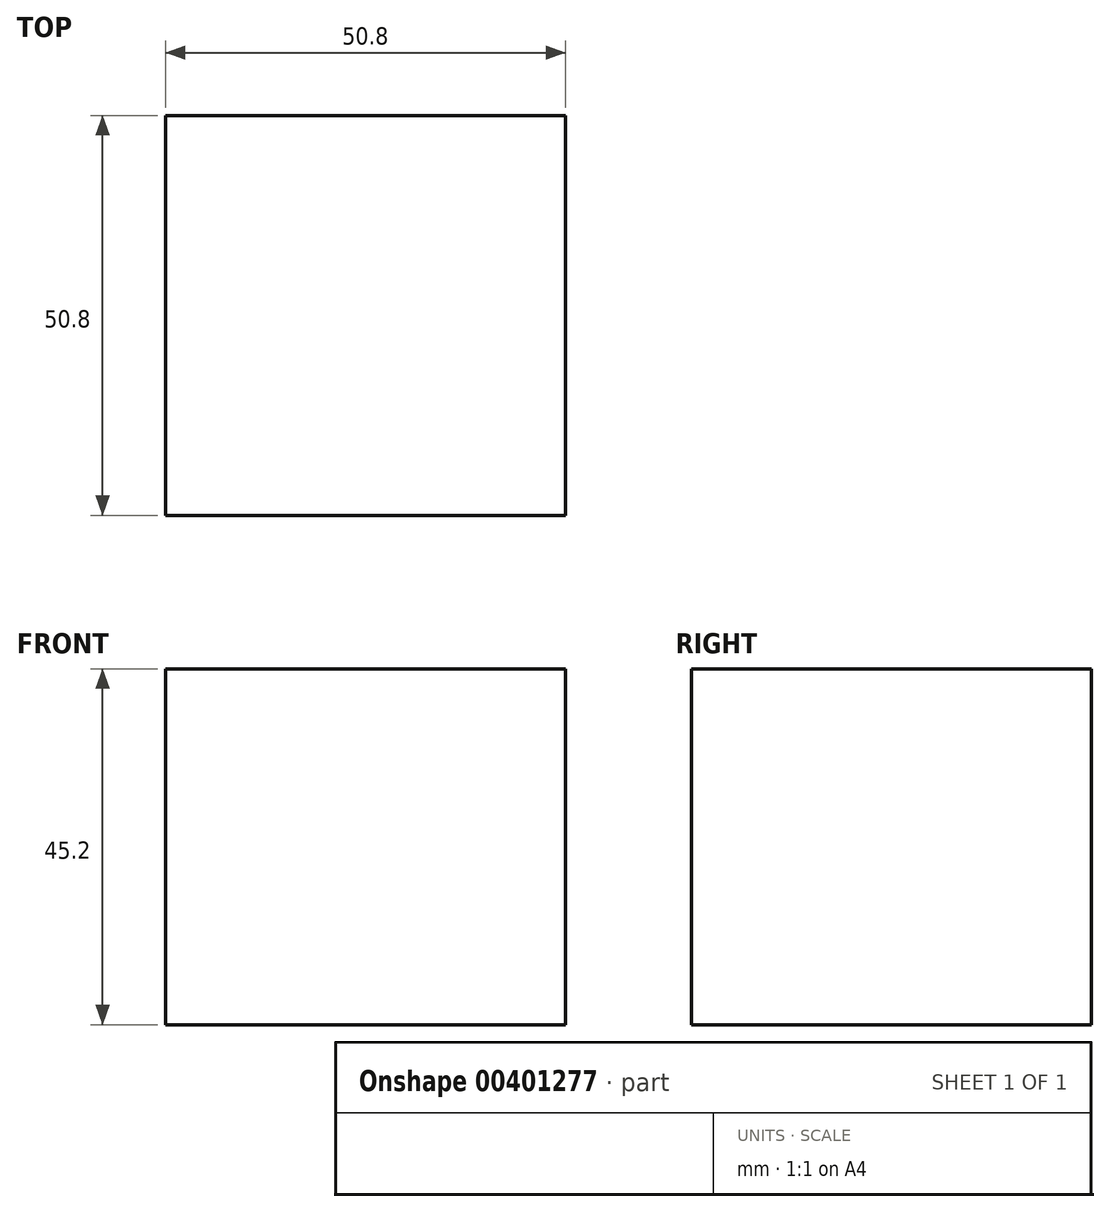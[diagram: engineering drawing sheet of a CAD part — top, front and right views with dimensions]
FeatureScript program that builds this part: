
annotation { "Feature Type Name" : "Feature", "Feature Type Description" : "" }
export const myFeature = defineFeature(function(context is Context, id is Id, definition is map)
    precondition{}
    {
        {
            var Q0;
            Q0=qCreatedBy(makeId("Front.planeOp"),FACE);
            var sketch = newSketch(context, id + "F0", { "sketchPlane" : qUnion([Q0])});
            skLineSegment(sketch, "E0.bottom", {"start": v(-63.55, 62.4) * mm, "end": v(-12.75, 62.4) * mm});
            skLineSegment(sketch, "E0.top", {"start": v(-63.55, 17.2) * mm, "end": v(-12.75, 17.2) * mm});
            skLineSegment(sketch, "E0.left", {"start": v(-63.55, 62.4) * mm, "end": v(-63.55, 17.2) * mm});
            skLineSegment(sketch, "E0.right", {"start": v(-12.75, 62.4) * mm, "end": v(-12.75, 17.2) * mm});
            skSolve(sketch);
        }
        {
            var Q0;
            Q0=makeQuery(id+"F0.imprint","IMPRINT",FACE,{"disambiguationData":[TD([[makeQuery(id+"F0.imprint","IMPRINT",EDGE,{"derivedFrom":sQuery(id+"F0.wireOp",EDGE,"E0.bottom")}),-1.0]])]});
            extrude(context, id + "F1", {"entities" : qUnion([Q0]), "depth" : 50.8 * mm});
        }
    });
